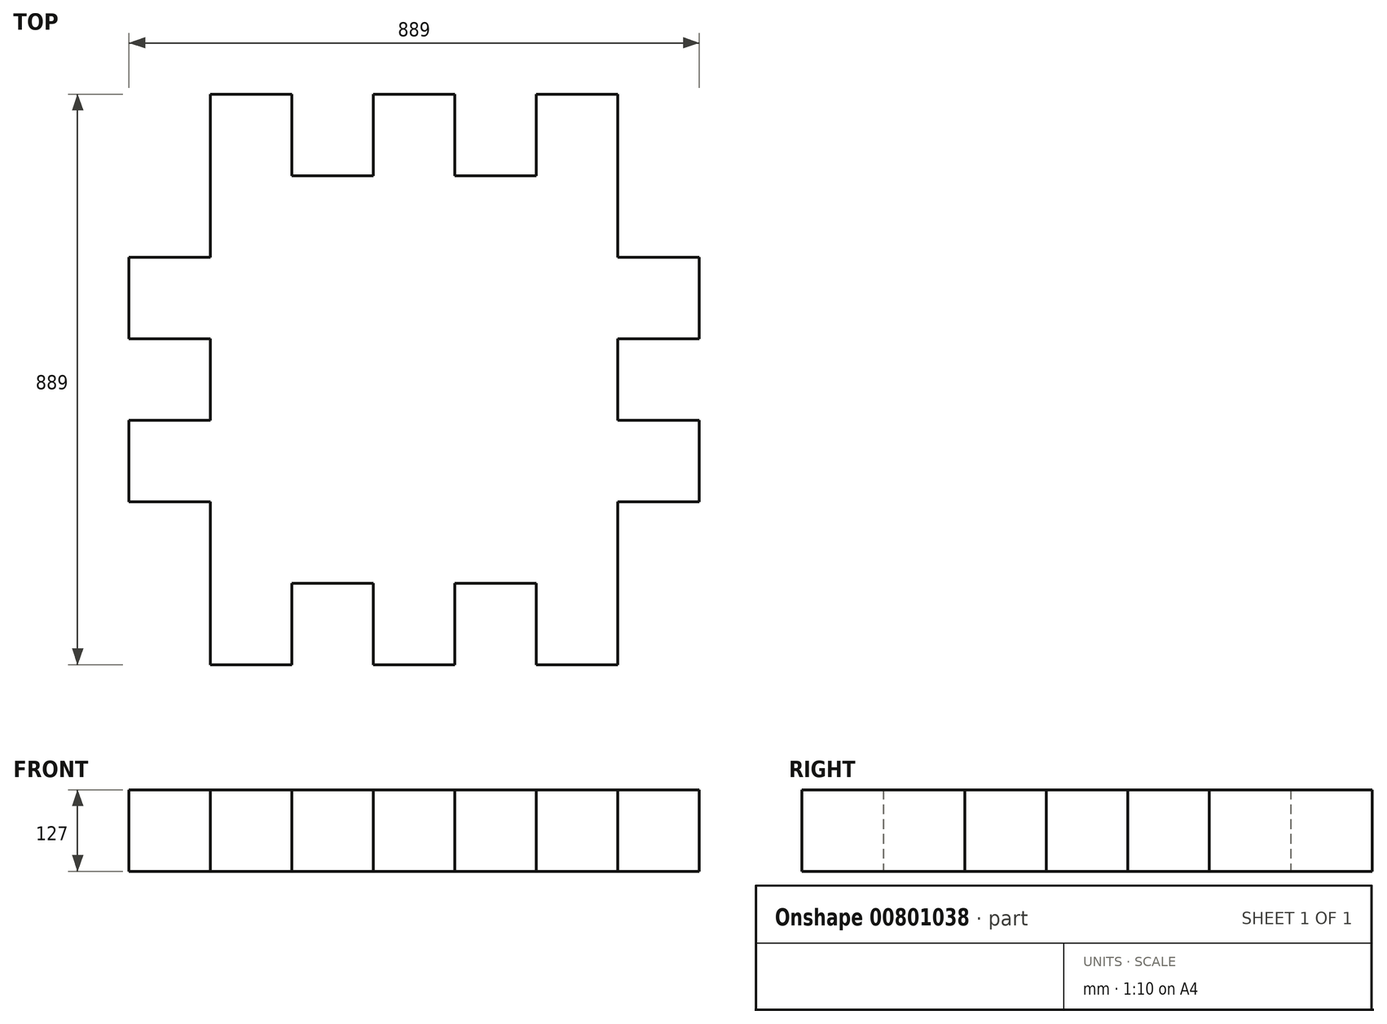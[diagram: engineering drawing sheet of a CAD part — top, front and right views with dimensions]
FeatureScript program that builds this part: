
annotation { "Feature Type Name" : "Feature", "Feature Type Description" : "" }
export const myFeature = defineFeature(function(context is Context, id is Id, definition is map)
    precondition{}
    {
        {
            var Q0;
            Q0=qCreatedBy(makeId("Top.planeOp"),FACE);
            var sketch = newSketch(context, id + "F0", { "sketchPlane" : qUnion([Q0])});
            skLineSegment(sketch, "E0.bottom", {"start": v(0, 0) * mm, "end": v(635, 0) * mm});
            skLineSegment(sketch, "E0.top", {"start": v(0, -635) * mm, "end": v(635, -635) * mm});
            skLineSegment(sketch, "E0.left", {"start": v(0, 0) * mm, "end": v(0, -635) * mm});
            skLineSegment(sketch, "E0.right", {"start": v(635, 0) * mm, "end": v(635, -635) * mm});
            skLineSegment(sketch, "E1.bottom", {"start": v(0, 0) * mm, "end": v(127, 0) * mm});
            skLineSegment(sketch, "E1.top", {"start": v(0, 127) * mm, "end": v(127, 127) * mm});
            skLineSegment(sketch, "E1.left", {"start": v(0, 0) * mm, "end": v(0, 127) * mm});
            skLineSegment(sketch, "E1.right", {"start": v(127, 0) * mm, "end": v(127, 127) * mm});
            skLineSegment(sketch, "E2.bottom", {"start": v(254, 0) * mm, "end": v(381, 0) * mm});
            skLineSegment(sketch, "E2.top", {"start": v(254, 127) * mm, "end": v(381, 127) * mm});
            skLineSegment(sketch, "E2.left", {"start": v(254, 0) * mm, "end": v(254, 127) * mm});
            skLineSegment(sketch, "E2.right", {"start": v(381, 0) * mm, "end": v(381, 127) * mm});
            skLineSegment(sketch, "E3.bottom", {"start": v(635, 0) * mm, "end": v(508, 0) * mm});
            skLineSegment(sketch, "E3.top", {"start": v(635, 127) * mm, "end": v(508, 127) * mm});
            skLineSegment(sketch, "E3.left", {"start": v(635, 0) * mm, "end": v(635, 127) * mm});
            skLineSegment(sketch, "E3.right", {"start": v(508, 0) * mm, "end": v(508, 127) * mm});
            skLineSegment(sketch, "E4.bottom", {"start": v(635, -127) * mm, "end": v(762, -127) * mm});
            skLineSegment(sketch, "E4.top", {"start": v(635, -254) * mm, "end": v(762, -254) * mm});
            skLineSegment(sketch, "E4.left", {"start": v(635, -127) * mm, "end": v(635, -254) * mm});
            skLineSegment(sketch, "E4.right", {"start": v(762, -127) * mm, "end": v(762, -254) * mm});
            skLineSegment(sketch, "E5.bottom", {"start": v(635, -381) * mm, "end": v(762, -381) * mm});
            skLineSegment(sketch, "E5.top", {"start": v(635, -508) * mm, "end": v(762, -508) * mm});
            skLineSegment(sketch, "E5.left", {"start": v(635, -381) * mm, "end": v(635, -508) * mm});
            skLineSegment(sketch, "E5.right", {"start": v(762, -381) * mm, "end": v(762, -508) * mm});
            skLineSegment(sketch, "E6.bottom", {"start": v(0, -635) * mm, "end": v(127, -635) * mm});
            skLineSegment(sketch, "E6.top", {"start": v(0, -762) * mm, "end": v(127, -762) * mm});
            skLineSegment(sketch, "E6.left", {"start": v(0, -635) * mm, "end": v(0, -762) * mm});
            skLineSegment(sketch, "E6.right", {"start": v(127, -635) * mm, "end": v(127, -762) * mm});
            skLineSegment(sketch, "E7.bottom", {"start": v(254, -635) * mm, "end": v(381, -635) * mm});
            skLineSegment(sketch, "E7.top", {"start": v(254, -762) * mm, "end": v(381, -762) * mm});
            skLineSegment(sketch, "E7.left", {"start": v(254, -635) * mm, "end": v(254, -762) * mm});
            skLineSegment(sketch, "E7.right", {"start": v(381, -635) * mm, "end": v(381, -762) * mm});
            skLineSegment(sketch, "E8.bottom", {"start": v(635, -635) * mm, "end": v(508, -635) * mm});
            skLineSegment(sketch, "E8.top", {"start": v(635, -762) * mm, "end": v(508, -762) * mm});
            skLineSegment(sketch, "E8.left", {"start": v(635, -635) * mm, "end": v(635, -762) * mm});
            skLineSegment(sketch, "E8.right", {"start": v(508, -635) * mm, "end": v(508, -762) * mm});
            skLineSegment(sketch, "E9.bottom", {"start": v(0, -127) * mm, "end": v(-127, -127) * mm});
            skLineSegment(sketch, "E9.top", {"start": v(0, -254) * mm, "end": v(-127, -254) * mm});
            skLineSegment(sketch, "E9.left", {"start": v(0, -127) * mm, "end": v(0, -254) * mm});
            skLineSegment(sketch, "E9.right", {"start": v(-127, -127) * mm, "end": v(-127, -254) * mm});
            skLineSegment(sketch, "E10.bottom", {"start": v(0, -381) * mm, "end": v(-127, -381) * mm});
            skLineSegment(sketch, "E10.top", {"start": v(0, -508) * mm, "end": v(-127, -508) * mm});
            skLineSegment(sketch, "E10.left", {"start": v(0, -381) * mm, "end": v(0, -508) * mm});
            skLineSegment(sketch, "E10.right", {"start": v(-127, -381) * mm, "end": v(-127, -508) * mm});
            skSolve(sketch);
        }
        {
            var Q0;
            Q0 = qSketchRegion(id + "F0", true);
            extrude(context, id + "F1", {"entities" : qUnion([Q0]), "depth" : 127 * mm, "offsetDistance" : 25.4 * mm});
        }
    });
